# Revit family: Pressure_Reducing_Valves-Acorn-Controls-RV03B0-X_Series
name_source: partatom
category: Pipe Accessories
units: mm (PartAtom-declared; Revit-internal decimal feet)

## family parameters
Always vertical = Yes
Cut with Voids When Loaded = No
OmniClass Number = 23.65.55.14.17
OmniClass Title = Adjusting/Controlling Valves for Liquid Services
Part Type = Valve - Breaks Into
Round Connector Dimension = Use Diameter
Shared = No
Work Plane-Based = No

## types (5) — shared parameters
Adapter 0 None = Yes
Adapter A Sweat = No
Adapter B NPTF = No
Adapter C PEX-B = No
Adapter D CPVC = No
Adapter E Press Fit = No
Adapter F PEX-A = No
Adjustable Pressure Range (High Pressure) = 30-120 PSI (207-827 kPa)
Adjustable Pressure Range (Standard) = 10-75 PSI (69-517 kPa)
Assembly Code = D2090900
B Constraint = 1/4"
B Dimension = 0"
B0 Brass = Yes
BH Brass HP - High Pressure Spring = No
Body Material = Metal-Acorn-Brass
Bonnet Material = Metal-Acorn-UV Resistant-Brass
Description = Pressure Reducing Valves
Factory Preset = 50±5 PSI (345kPa)
IAPMO Compliance = Comply with the national lead-free law, ASSE 1003 & NSF-61.
Installation Instruction Link = https://www.mgicontrols.com
Manufacturer = Acorn
P0 Plastic = No
PH Plastic HP - High Pressure Spring = No
Pressure Gauge 0 No Gauge Adapter = Yes
Pressure Gauge G Adapter With 0-200 psi Gauge = No
Pressure Gauge T Adapter with 1/4” Plug (No Gauge) = No
Pressure Rating = 400 PSI (2758 kPa)
Product Documentation Link = https://www.mgicontrols.com
Product Page URL = https://www.mgicontrols.com
Revised Date = 02/04/2025
S0 Steel = No
SH Steel HP - High Pressure Spring = No
Temperature Rating = 180°F (82.2°C)
URL = https://www.acorneng.com
cUPC Compliant = Yes

## per-type parameters (varying)
| type | A Dimension | Connection Inlet Description | Connection Outlet Description | D Constraint | D Constraint 2 | D Dimension | E Dimension | Valve Size | Valve Size 2 | Valve Size 3 | Valve Size 4 | Valve Size 5 | Valve Size 6 |
| RV03B0-2 | 3 3/8" | 3/4-in Inlet Connection | 3/4-in Outlet Connection | 1 3/4" | 2 3/8" | 1 5/8" | 4 3/4" | 3/4" | Yes | No | No | No | No |
| RV03B0-3 | 3 7/8" | 1-in Inlet Connection | 1-in Outlet Connection | 2" | 2 5/8" | 1 7/8" | 5 1/2" | 1" | No | Yes | No | No | No |
| RV03B0-4 | 5" | 1 1/4-in Inlet Connection | 1 1/4-in Outlet Connection | 2 1/2" | 3 1/8" | 2 3/8" | 8 1/8" | 1 1/4" | No | No | Yes | No | No |
| RV03B0-5 | 5" | 1 1/2-in Inlet Connection | 1 1/2-in Outlet Connection | 3" | 3 5/8" | 2 7/8" | 8 1/8" | 1 1/2" | No | No | No | Yes | No |
| RV03B0-6 | 5" | 2-in Inlet Connection | 2-in Outlet Connection | 3 5/8" | 4 1/4" | 3 1/2" | 8 1/8" | 2" | No | No | No | No | Yes |

note: column(s) folded — value = type name in every type: Model

## geometry (parser evidence)
native form markers: Sweep x2
no freeform markers — native parametric forms only
